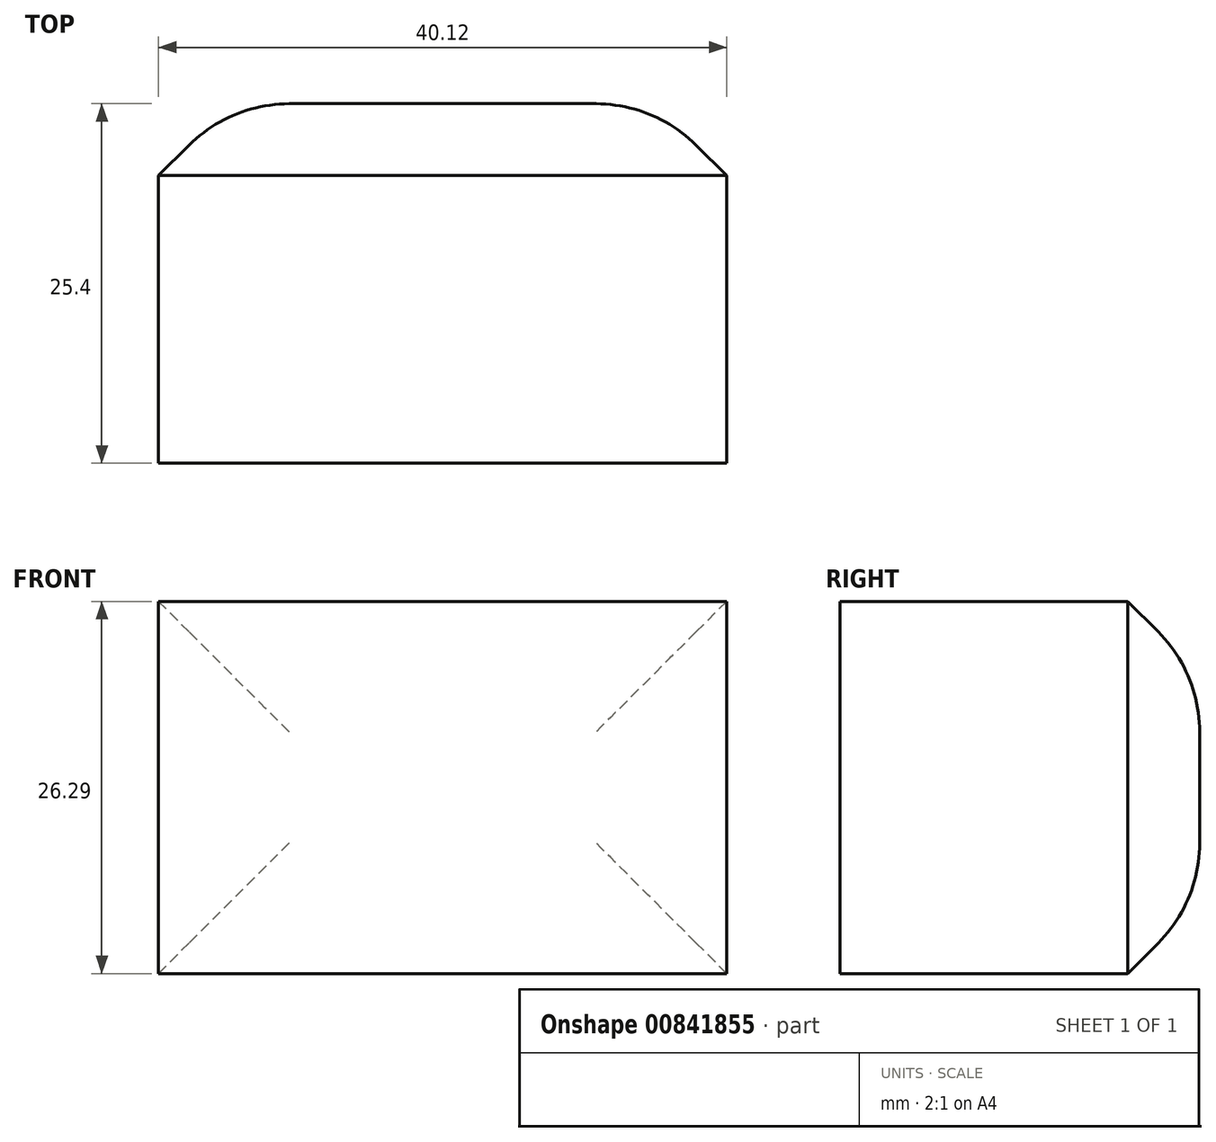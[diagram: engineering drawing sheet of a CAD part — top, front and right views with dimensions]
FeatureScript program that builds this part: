
annotation { "Feature Type Name" : "Feature", "Feature Type Description" : "" }
export const myFeature = defineFeature(function(context is Context, id is Id, definition is map)
    precondition{}
    {
        {
            var Q0;
            Q0=qCreatedBy(makeId("Front.planeOp"),FACE);
            var sketch = newSketch(context, id + "F0", { "sketchPlane" : qUnion([Q0])});
            skLineSegment(sketch, "E0.bottom", {"start": v(40.12, 39.24) * mm, "end": v(0, 39.24) * mm});
            skLineSegment(sketch, "E0.top", {"start": v(40.12, 12.95) * mm, "end": v(0, 12.95) * mm});
            skLineSegment(sketch, "E0.left", {"start": v(40.12, 39.24) * mm, "end": v(40.12, 12.95) * mm});
            skLineSegment(sketch, "E0.right", {"start": v(0, 39.24) * mm, "end": v(0, 12.95) * mm});
            skSolve(sketch);
        }
        {
            var Q0;
            Q0=makeQuery(id+"F0.imprint","IMPRINT",FACE,{"disambiguationData":[TD([[makeQuery(id+"F0.imprint","IMPRINT",EDGE,{"derivedFrom":sQuery(id+"F0.wireOp",EDGE,"E0.bottom")}),1.0]])]});
            extrude(context, id + "F1", {"entities" : qUnion([Q0]), "depth" : 25.4 * mm, "offsetDistance" : 25.4 * mm});
        }
        {
            var Q0;
            Q0=makeQuery(id+"F1.opExtrude","CAP_FACE",FACE,{"disambiguationData":[OSD([sQuery(id+"F0.wireOp",EDGE,"E0.bottom"),sQuery(id+"F0.wireOp",EDGE,"E0.top"),sQuery(id+"F0.wireOp",EDGE,"E0.left"),sQuery(id+"F0.wireOp",EDGE,"E0.right")])],"isStart":true});
            chamfer(context, id + "F2", {"entities" : qUnion([Q0]), "width" : 5.08 * mm, "tangentPropagation" : true});
        }
        {
            var Q0;
            {var subQ0=sQuery(id+"F0.wireOp",EDGE,"E0.left");Q0=makeQuery(id+"F2.opChamfer","BLEND_EDGE",EDGE,{"blendedFrom":[makeQuery(id+"F1.opExtrude","CAP_EDGE",EDGE,{"disambiguationData":[OSD([subQ0])],"isStart":true}),makeQuery(id+"F1.opExtrude","CAP_FACE",FACE,{"disambiguationData":[OSD([sQuery(id+"F0.wireOp",EDGE,"E0.bottom"),sQuery(id+"F0.wireOp",EDGE,"E0.top"),subQ0,sQuery(id+"F0.wireOp",EDGE,"E0.right")])],"isStart":true})],"blendedInto":[makeQuery(id+"F1.opExtrude","CAP_FACE",FACE,{"disambiguationData":[OSD([sQuery(id+"F0.wireOp",EDGE,"E0.bottom"),sQuery(id+"F0.wireOp",EDGE,"E0.top"),subQ0,sQuery(id+"F0.wireOp",EDGE,"E0.right")])],"isStart":true})]});}
            var Q1;
            {var subQ0=sQuery(id+"F0.wireOp",EDGE,"E0.bottom");Q1=makeQuery(id+"F2.opChamfer","BLEND_EDGE",EDGE,{"blendedFrom":[makeQuery(id+"F1.opExtrude","CAP_EDGE",EDGE,{"disambiguationData":[OSD([subQ0])],"isStart":true}),makeQuery(id+"F1.opExtrude","CAP_FACE",FACE,{"disambiguationData":[OSD([subQ0,sQuery(id+"F0.wireOp",EDGE,"E0.top"),sQuery(id+"F0.wireOp",EDGE,"E0.left"),sQuery(id+"F0.wireOp",EDGE,"E0.right")])],"isStart":true})],"blendedInto":[makeQuery(id+"F1.opExtrude","CAP_FACE",FACE,{"disambiguationData":[OSD([subQ0,sQuery(id+"F0.wireOp",EDGE,"E0.top"),sQuery(id+"F0.wireOp",EDGE,"E0.left"),sQuery(id+"F0.wireOp",EDGE,"E0.right")])],"isStart":true})]});}
            var Q2;
            {var subQ0=sQuery(id+"F0.wireOp",EDGE,"E0.right");Q2=makeQuery(id+"F2.opChamfer","BLEND_EDGE",EDGE,{"blendedFrom":[makeQuery(id+"F1.opExtrude","CAP_EDGE",EDGE,{"disambiguationData":[OSD([subQ0])],"isStart":true}),makeQuery(id+"F1.opExtrude","CAP_FACE",FACE,{"disambiguationData":[OSD([sQuery(id+"F0.wireOp",EDGE,"E0.bottom"),sQuery(id+"F0.wireOp",EDGE,"E0.top"),sQuery(id+"F0.wireOp",EDGE,"E0.left"),subQ0])],"isStart":true})],"blendedInto":[makeQuery(id+"F1.opExtrude","CAP_FACE",FACE,{"disambiguationData":[OSD([sQuery(id+"F0.wireOp",EDGE,"E0.bottom"),sQuery(id+"F0.wireOp",EDGE,"E0.top"),sQuery(id+"F0.wireOp",EDGE,"E0.left"),subQ0])],"isStart":true})]});}
            var Q3;
            {var subQ0=sQuery(id+"F0.wireOp",EDGE,"E0.top");Q3=makeQuery(id+"F2.opChamfer","BLEND_EDGE",EDGE,{"blendedFrom":[makeQuery(id+"F1.opExtrude","CAP_EDGE",EDGE,{"disambiguationData":[OSD([subQ0])],"isStart":true}),makeQuery(id+"F1.opExtrude","CAP_FACE",FACE,{"disambiguationData":[OSD([sQuery(id+"F0.wireOp",EDGE,"E0.bottom"),subQ0,sQuery(id+"F0.wireOp",EDGE,"E0.left"),sQuery(id+"F0.wireOp",EDGE,"E0.right")])],"isStart":true})],"blendedInto":[makeQuery(id+"F1.opExtrude","CAP_FACE",FACE,{"disambiguationData":[OSD([sQuery(id+"F0.wireOp",EDGE,"E0.bottom"),subQ0,sQuery(id+"F0.wireOp",EDGE,"E0.left"),sQuery(id+"F0.wireOp",EDGE,"E0.right")])],"isStart":true})]});}
            fillet(context, id + "F3", {"entities" : qUnion([Q0, Q1, Q2, Q3]), "radius" : 10 * mm, "tangentPropagation" : true, "allowEdgeOverflow" : false});
        }
    });
